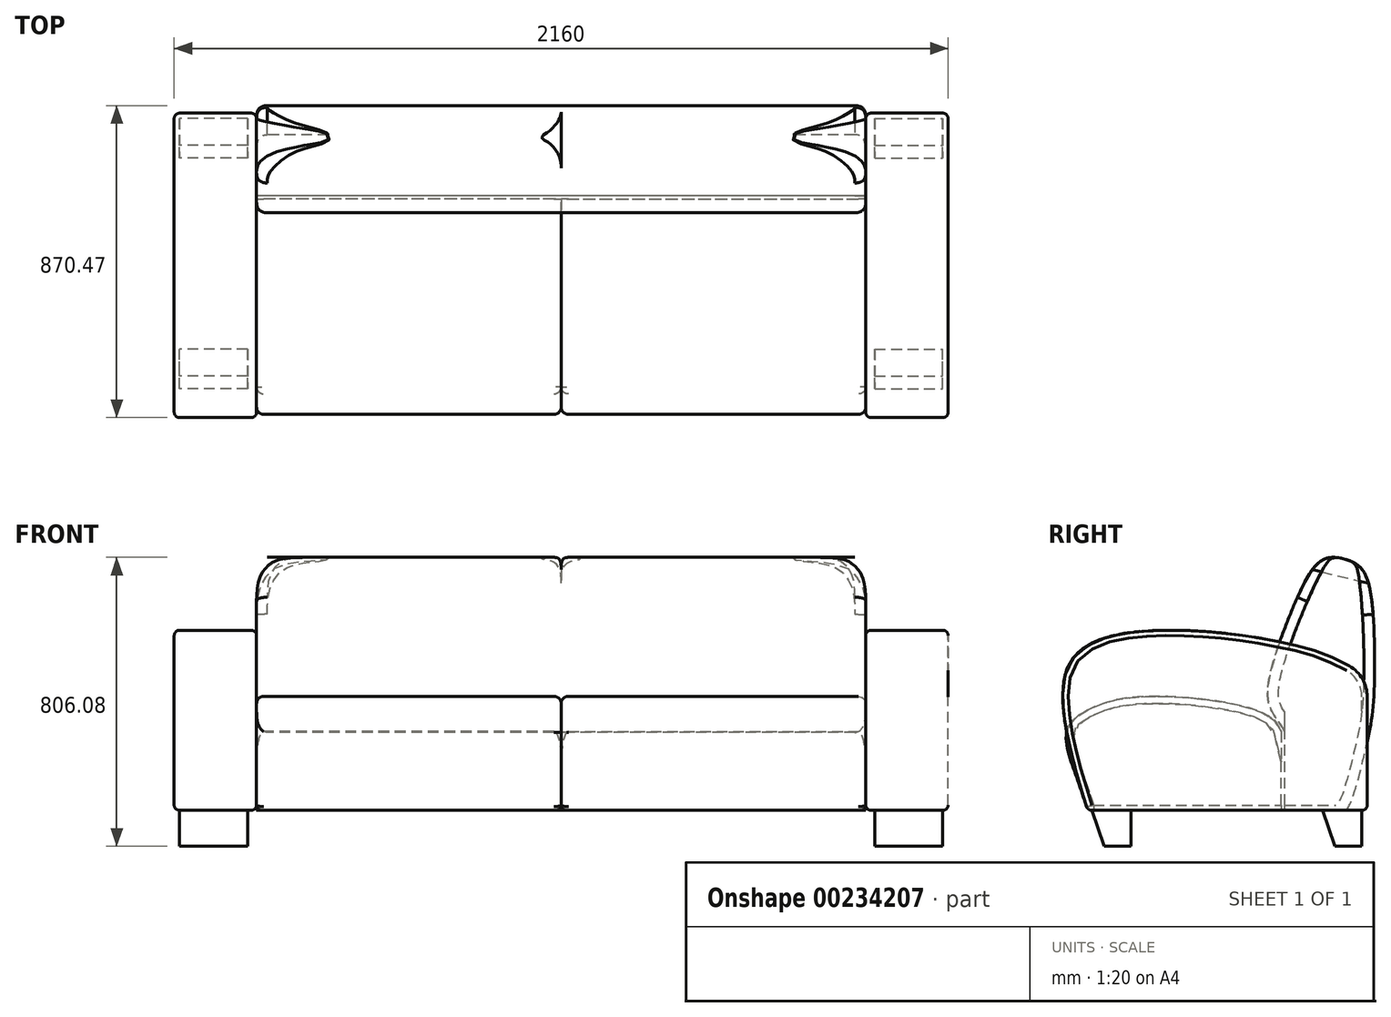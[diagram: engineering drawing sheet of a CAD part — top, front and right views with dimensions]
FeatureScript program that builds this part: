
annotation { "Feature Type Name" : "Feature", "Feature Type Description" : "" }
export const myFeature = defineFeature(function(context is Context, id is Id, definition is map)
    precondition{}
    {
        {
            var Q0;
            Q0=qCreatedBy(makeId("Right.planeOp"),FACE);
            var sketch = newSketch(context, id + "F0", { "sketchPlane" : qUnion([Q0])});
            skLineSegment(sketch, "E0", {"start": v(0, 0) * mm, "end": v(0, 316.61) * mm});
            skFitSpline(sketch, "E1", {"points": [v(0, 370) * mm, v(-204.49, 461.59) * mm, v(-625.47, 500) * mm, v(-838.22, 392.55) * mm, v(-780, 0) * mm], "startDerivative": vector(-907.82, 674.11) * mm, "endDerivative": vector(397.14, -1314.97) * mm});
            skLineSegment(sketch, "E2", {"start": v(-780, 0) * mm, "end": v(0, 0) * mm});
            skArc(sketch, "E3.filletArc", {"start": v(0, 316.61) * mm, "mid": v(-13.27, 366.4) * mm, "end": v(-49.57, 402.96) * mm});
            skSolve(sketch);
        }
        {
            var Q0;
            Q0 = qSketchRegion(id + "F0", true);
            extrude(context, id + "F1", {"entities" : qUnion([Q0]), "depth" : 230 * mm});
        }
        {
            var Q0;
            Q0=makeQuery(id+"F1.opExtrude","CAP_FACE",FACE,{"disambiguationData":[OSD([sQuery(id+"F0.wireOp",EDGE,"E0"),sQuery(id+"F0.wireOp",EDGE,"E1"),sQuery(id+"F0.wireOp",EDGE,"E2"),sQuery(id+"F0.wireOp",EDGE,"E3.filletArc")])],"isStart":false});
            var Q1;
            Q1=makeQuery(id+"F1.opExtrude","CAP_FACE",FACE,{"disambiguationData":[OSD([sQuery(id+"F0.wireOp",EDGE,"E0"),sQuery(id+"F0.wireOp",EDGE,"E1"),sQuery(id+"F0.wireOp",EDGE,"E2"),sQuery(id+"F0.wireOp",EDGE,"E3.filletArc")])],"isStart":true});
            var Q2;
            Q2=makeQuery(id+"F1.opExtrude","SWEPT_FACE",FACE,{"disambiguationData":[OSD([sQuery(id+"F0.wireOp",EDGE,"E2")])]});
            fillet(context, id + "F2", {"entities" : qUnion([Q0, Q1, Q2]), "radius" : 15 * mm, "tangentPropagation" : true, "allowEdgeOverflow" : false});
        }
        {
            var Q0;
            Q0=makeQuery(id+"F1.opExtrude","CAP_FACE",FACE,{"disambiguationData":[OSD([sQuery(id+"F0.wireOp",EDGE,"E0"),sQuery(id+"F0.wireOp",EDGE,"E1"),sQuery(id+"F0.wireOp",EDGE,"E2"),sQuery(id+"F0.wireOp",EDGE,"E3.filletArc")])],"isStart":false});
            var sketch = newSketch(context, id + "F3", { "sketchPlane" : qUnion([Q0])});
            skLineSegment(sketch, "E4", {"start": v(-780, 0) * mm, "end": v(-240, 0) * mm});
            skLineSegment(sketch, "E5", {"start": v(-240, 0) * mm, "end": v(-240, 220) * mm});
            skFitSpline(sketch, "E6", {"points": [v(-240, 220) * mm, v(-285.68, 269.16) * mm, v(-472.6, 311.85) * mm, v(-682.71, 311.82) * mm, v(-787.13, 276.42) * mm, v(-839, 220) * mm, v(-780, 0) * mm], "startDerivative": vector(-128.74, 527.1) * mm, "endDerivative": vector(392.08, -1310.55) * mm});
            skSolve(sketch);
        }
        {
            var Q0;
            Q0 = qSketchRegion(id + "F3", true);
            extrude(context, id + "F4", {"entities" : qUnion([Q0]), "depth" : 850 * mm});
        }
        {
            var Q0;
            Q0=makeQuery(id+"F4.opExtrude","CAP_EDGE",EDGE,{"disambiguationData":[OSD([sQuery(id+"F3.wireOp",EDGE,"E6")])],"isStart":true});
            var Q1;
            Q1=makeQuery(id+"F4.opExtrude","CAP_EDGE",EDGE,{"disambiguationData":[OSD([sQuery(id+"F3.wireOp",EDGE,"E6")])],"isStart":false});
            fillet(context, id + "F5", {"entities" : qUnion([Q0, Q1]), "radius" : 20 * mm, "tangentPropagation" : true, "allowEdgeOverflow" : false});
        }
        {
            var Q0;
            Q0=makeQuery(id+"F4.opExtrude","SWEPT_EDGE",EDGE,{"disambiguationData":[OSD([sQuery(id+"F3.wireOp",EDGE,"E4"),sQuery(id+"F3.wireOp",EDGE,"E6")])]});
            fillet(context, id + "F6", {"entities" : qUnion([Q0]), "radius" : 15 * mm, "tangentPropagation" : true, "allowEdgeOverflow" : false});
        }
        {
            var Q0;
            Q0=makeQuery(id+"F1.opExtrude","CAP_FACE",FACE,{"disambiguationData":[OSD([sQuery(id+"F0.wireOp",EDGE,"E0"),sQuery(id+"F0.wireOp",EDGE,"E1"),sQuery(id+"F0.wireOp",EDGE,"E2"),sQuery(id+"F0.wireOp",EDGE,"E3.filletArc")])],"isStart":false});
            var sketch = newSketch(context, id + "F7", { "sketchPlane" : qUnion([Q0])});
            skLineSegment(sketch, "E7", {"start": v(-60, 0) * mm, "end": v(-230, 0) * mm});
            skLineSegment(sketch, "E8", {"start": v(-230, 0) * mm, "end": v(-230, 218.02) * mm});
            skPoint(sketch, "E9.5.internal.snap0", {"position": v(-15, 165.8) * mm});
            skFitSpline(sketch, "E9", {"points": [v(-60, 0) * mm, v(-44.95, 24.05) * mm, v(-5.64, 165.8) * mm, v(16.03, 284.89) * mm, v(19.64, 484.26) * mm, v(-10.02, 666.35) * mm, v(-60, 700.45) * mm, v(-107.78, 705) * mm, v(-144.75, 682.32) * mm, v(-208.13, 563.48) * mm, v(-277.45, 339.68) * mm, v(-261.93, 268.56) * mm, v(-230, 218.02) * mm], "startDerivative": vector(377.89, 382.41) * mm, "endDerivative": vector(388.26, -831.24) * mm});
            skLineSegment(sketch, "E10", {"start": v(-60, 700.45) * mm, "end": v(-230, 0) * mm, "construction": true});
            skLineSegment(sketch, "E11", {"start": v(-66.15, 705) * mm, "end": v(-120.13, 482.6) * mm, "construction": true});
            skSolve(sketch);
        }
        {
            var Q0;
            Q0=sQuery(id+"F7.wireOp",EDGE,"E11");
            cPlane(context, id + "F8", {"entities" : qUnion([Q0]), "cplaneType" : CPlaneType.LINE_ANGLE, "offset" : 25 * mm, "angle" : 90 * degree, "width" : 150 * mm, "height" : 150 * mm});
        }
        {
            var Q0;
            Q0 = qSketchRegion(id + "F7", true);
            var Q1;
            Q1=makeQuery(id+"F4.opExtrude","CAP_FACE",FACE,{"disambiguationData":[OSD([sQuery(id+"F3.wireOp",EDGE,"E4"),sQuery(id+"F3.wireOp",EDGE,"E5"),sQuery(id+"F3.wireOp",EDGE,"E6")])],"isStart":false});
            extrude(context, id + "F9", {"entities" : qUnion([Q0]), "endBound" : BoundingType.UP_TO_SURFACE, "endBoundEntityFace" : qUnion([Q1]), "depth" : 25 * mm});
        }
        {
            var Q0;
            Q0=qCreatedBy(id+"F8.planeOp",FACE);
            var sketch = newSketch(context, id + "F10", { "sketchPlane" : qUnion([Q0])});
            skLineSegment(sketch, "E12", {"start": v(-230, 666.54) * mm, "end": v(-440, 666.54) * mm, "construction": true});
            skLineSegment(sketch, "E13", {"start": v(-230, 666.54) * mm, "end": v(-230, 526.54) * mm});
            skLineSegment(sketch, "E14", {"start": v(-1020, 666.84) * mm, "end": v(-1080, 666.84) * mm});
            skLineSegment(sketch, "E15", {"start": v(-1080, 666.84) * mm, "end": v(-1080, 616.84) * mm});
            skFitSpline(sketch, "E16", {"points": [v(-1020, 666.84) * mm, v(-1051.75, 665.18) * mm, v(-1068.28, 659.72) * mm, v(-1077.37, 645.6) * mm, v(-1080, 616.84) * mm], "startDerivative": vector(-207.29, -5.6) * mm, "endDerivative": vector(0, -128.27) * mm});
            skFitSpline(sketch, "E17", {"points": [v(-230, 526.54) * mm, v(-232, 569.07) * mm, v(-238.1, 595.37) * mm, v(-247.46, 616.68) * mm, v(-275.48, 646.13) * mm, v(-322.23, 660.52) * mm, v(-374.92, 664.54) * mm, v(-440, 666.84) * mm], "startDerivative": vector(0, 508.12) * mm, "endDerivative": vector(-408.08, 15.69) * mm});
            skLineSegment(sketch, "E18", {"start": v(-230, 666.54) * mm, "end": v(-230, 666.84) * mm});
            skLineSegment(sketch, "E19", {"start": v(-230, 666.84) * mm, "end": v(-440, 666.84) * mm});
            skLineSegment(sketch, "E20", {"start": v(-440, 666.84) * mm, "end": v(-440, 666.54) * mm});
            skSolve(sketch);
        }
        {
            var Q0;
            Q0 = qSketchRegion(id + "F10", true);
            extrude(context, id + "F11", {"entities" : qUnion([Q0]), "operationType" : NewBodyOperationType.REMOVE, "endBound" : BoundingType.SYMMETRIC, "oppositeDirection" : true, "depth" : 426 * mm});
        }
        {
            var Q0;
            {var subQ0=sQuery(id+"F7.wireOp",EDGE,"E9");var subQ1=sQuery(id+"F7.wireOp",EDGE,"E8");Q0=makeQuery(id+"F11.boolean.opBoolean","SPLIT",EDGE,{"disambiguationData":[TD([makeQuery(id+"F9.opExtrude","SWEPT_FACE",FACE,{"disambiguationData":[OSD([subQ1])]})])],"derivedFrom":makeQuery(id+"F9.opExtrude","CAP_EDGE",EDGE,{"disambiguationData":[OSD([subQ0])],"isStart":true})});}
            var Q1;
            {var subQ0=sQuery(id+"F3.wireOp",EDGE,"E6");var subQ1=sQuery(id+"F3.wireOp",EDGE,"E5");var subQ2=sQuery(id+"F3.wireOp",EDGE,"E4");var subQ3=sQuery(id+"F7.wireOp",EDGE,"E9");var subQ4=sQuery(id+"F7.wireOp",EDGE,"E8");var subQ5=sQuery(id+"F0.wireOp",EDGE,"E2");var subQ6=sQuery(id+"F0.wireOp",EDGE,"E1");var subQ7=sQuery(id+"F0.wireOp",EDGE,"E0");var subQ8=makeQuery(id+"F1.opExtrude","CAP_FACE",FACE,{"disambiguationData":[OSD([subQ7,subQ6,subQ5,sQuery(id+"F0.wireOp",EDGE,"E3.filletArc")])],"isStart":false});var subQ10=makeQuery(id+"F7.imprint","INTERSECT",VERTEX,{"derivedFrom":[makeQuery(id+"F2.opFillet","BLEND_EDGE",EDGE,{"blendedFrom":[makeQuery(id+"F1.opExtrude","CAP_EDGE",EDGE,{"disambiguationData":[OSD([subQ7])],"isStart":false}),subQ8],"blendedInto":[subQ8]}),subQ3]});var subQ11=makeQuery(id+"F7.imprint","INTERSECT",VERTEX,{"derivedFrom":[makeQuery(id+"F2.opFillet","BLEND_EDGE",EDGE,{"blendedFrom":[makeQuery(id+"F1.opExtrude","CAP_EDGE",EDGE,{"disambiguationData":[OSD([subQ5])],"isStart":false}),subQ8],"blendedInto":[subQ8]}),subQ3]});Q1=makeQuery(id+"F11.boolean.opBoolean","SPLIT",EDGE,{"disambiguationData":[TD([makeQuery(id+"F9.opExtrude","SWEPT_FACE",FACE,{"disambiguationData":[OSD([subQ4])]})])],"derivedFrom":makeQuery(id+"F9.opExtrude","TWEAK_EDGE",EDGE,{"derivedFrom":[makeQuery(id+"F4.opExtrude","CAP_FACE",FACE,{"disambiguationData":[OSD([subQ2,subQ1,subQ0])],"isStart":false}),makeQuery(id+"F7.imprint","IMPRINT",EDGE,{"disambiguationData":[TD([[makeQuery(id+"F7.imprint","INTERSECT",VERTEX,{"derivedFrom":[sQuery(id+"F7.wireOp",EDGE,"E7"),subQ3]}),-1.0]])],"derivedFrom":subQ3}),makeQuery(id+"F7.imprint","IMPRINT",EDGE,{"disambiguationData":[TD([[subQ11,-1.0]])],"derivedFrom":subQ3}),makeQuery(id+"F7.imprint","IMPRINT",EDGE,{"disambiguationData":[TD([[subQ10,-1.0]])],"derivedFrom":subQ3}),makeQuery(id+"F7.imprint","IMPRINT",EDGE,{"disambiguationData":[TD([[makeQuery(id+"F7.imprint","INTERSECT",VERTEX,{"derivedFrom":[subQ4,subQ3]}),1.0]])],"derivedFrom":subQ3})]})});}
            fillet(context, id + "F12", {"entities" : qUnion([Q0, Q1]), "radius" : 30 * mm, "tangentPropagation" : true, "rho" : 0.5, "crossSection" : FilletCrossSection.CONIC, "allowEdgeOverflow" : false});
        }
        {
            var Q0;
            {var subQ0=sQuery(id+"F0.wireOp",EDGE,"E2");Q0=makeQuery(id+"F2.opFillet","BLEND_EDGE",EDGE,{"blendedFrom":[makeQuery(id+"F1.opExtrude","CAP_EDGE",EDGE,{"disambiguationData":[OSD([subQ0])],"isStart":true}),makeQuery(id+"F1.opExtrude","SWEPT_FACE",FACE,{"disambiguationData":[OSD([subQ0])]})],"blendedInto":[makeQuery(id+"F1.opExtrude","SWEPT_FACE",FACE,{"disambiguationData":[OSD([subQ0])]})]});}
            cPlane(context, id + "F13", {"entities" : qUnion([Q0]), "cplaneType" : CPlaneType.LINE_ANGLE, "offset" : 25 * mm, "angle" : 90 * degree, "width" : 150 * mm, "height" : 150 * mm});
        }
        {
            var Q0;
            Q0=qCreatedBy(id+"F13.planeOp",FACE);
            var sketch = newSketch(context, id + "F14", { "sketchPlane" : qUnion([Q0])});
            skLineSegment(sketch, "E21", {"start": v(-768.87, 0) * mm, "end": v(-733.87, -100) * mm});
            skLineSegment(sketch, "E22", {"start": v(-733.87, -100) * mm, "end": v(-658.87, -100) * mm});
            skLineSegment(sketch, "E23", {"start": v(-658.87, -100) * mm, "end": v(-658.87, 0) * mm});
            skLineSegment(sketch, "E24", {"start": v(-658.87, 0) * mm, "end": v(-768.87, 0) * mm});
            skLineSegment(sketch, "E25", {"start": v(-125, 0) * mm, "end": v(-90, -100) * mm});
            skLineSegment(sketch, "E26", {"start": v(-90, -100) * mm, "end": v(-15, -100) * mm});
            skLineSegment(sketch, "E27", {"start": v(-15, -100) * mm, "end": v(-15, 0) * mm});
            skLineSegment(sketch, "E28", {"start": v(-15, 0) * mm, "end": v(-125, 0) * mm});
            skSolve(sketch);
        }
        {
            var Q0;
            Q0 = qSketchRegion(id + "F14", true);
            extrude(context, id + "F15", {"entities" : qUnion([Q0]), "operationType" : NewBodyOperationType.ADD, "depth" : 190 * mm});
        }
        {
            var Q0;
            Q0=makeQuery(id+"F1.opExtrude","SWEPT_BODY",BODY,{"disambiguationData":[OSD([sQuery(id+"F0.wireOp",EDGE,"E0"),sQuery(id+"F0.wireOp",EDGE,"E1"),sQuery(id+"F0.wireOp",EDGE,"E2"),sQuery(id+"F0.wireOp",EDGE,"E3.filletArc")])]});
            var Q1;
            Q1=makeQuery(id+"F4.opExtrude","SWEPT_BODY",BODY,{"disambiguationData":[OSD([sQuery(id+"F3.wireOp",EDGE,"E4"),sQuery(id+"F3.wireOp",EDGE,"E5"),sQuery(id+"F3.wireOp",EDGE,"E6")])]});
            var Q2;
            Q2=makeQuery(id+"F9.opExtrude","SWEPT_BODY",BODY,{"disambiguationData":[OSD([sQuery(id+"F7.wireOp",EDGE,"E7"),sQuery(id+"F7.wireOp",EDGE,"E8"),sQuery(id+"F7.wireOp",EDGE,"E9")])]});
            var Q3;
            Q3=makeQuery(id+"F4.opExtrude","CAP_FACE",FACE,{"disambiguationData":[OSD([sQuery(id+"F3.wireOp",EDGE,"E4"),sQuery(id+"F3.wireOp",EDGE,"E5"),sQuery(id+"F3.wireOp",EDGE,"E6")])],"isStart":false});
            mirror(context, id + "F16", {"operationType" : NewBodyOperationType.ADD, "entities" : qUnion([Q0, Q1, Q2]), "mirrorPlane" : qUnion([Q3])});
        }
    });
